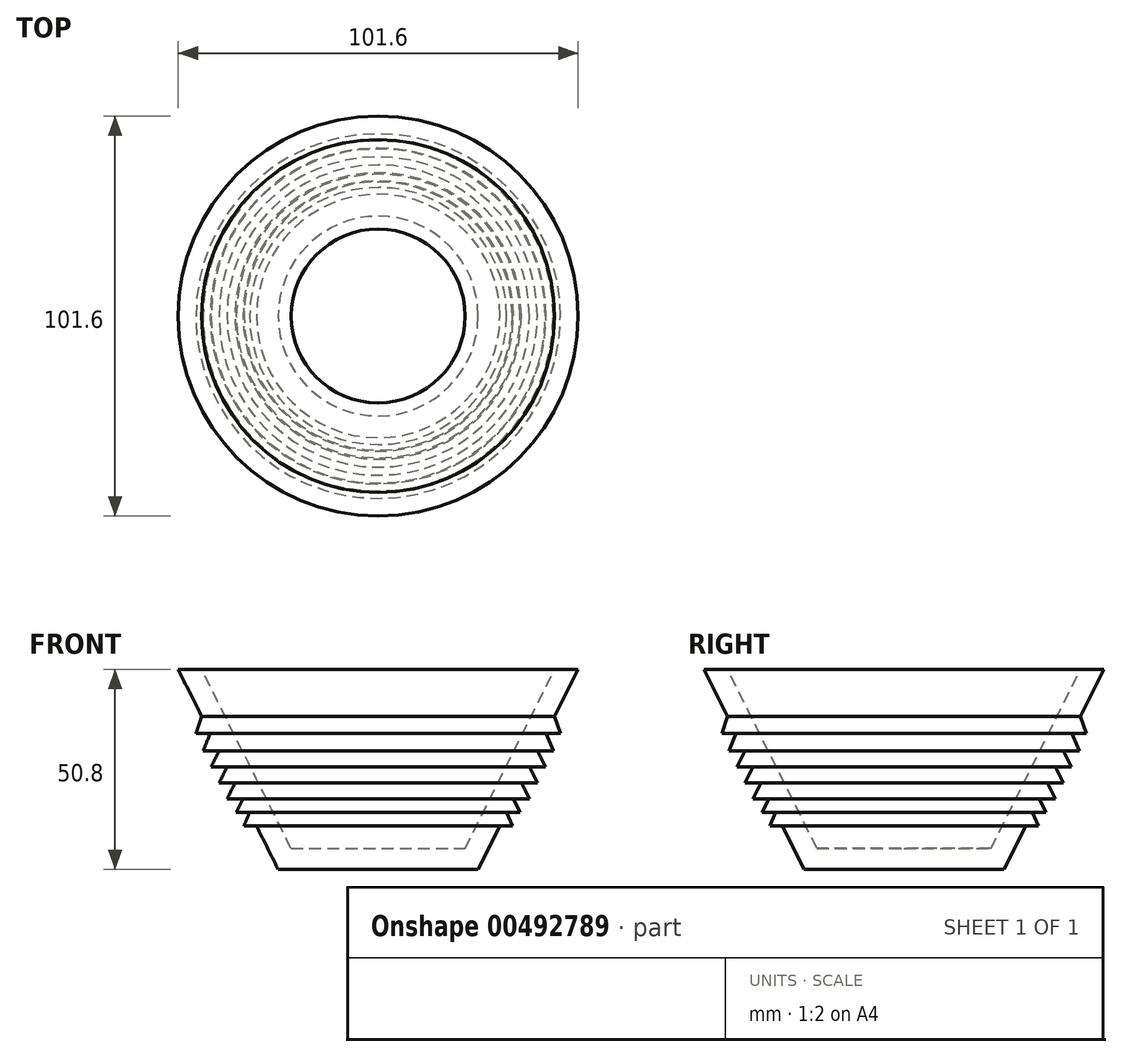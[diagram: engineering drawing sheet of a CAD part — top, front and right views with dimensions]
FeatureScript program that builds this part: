
annotation { "Feature Type Name" : "Feature", "Feature Type Description" : "" }
export const myFeature = defineFeature(function(context is Context, id is Id, definition is map)
    precondition{}
    {
        {
            var Q0;
            Q0=qCreatedBy(makeId("Front.planeOp"),FACE);
            var sketch = newSketch(context, id + "F0", { "sketchPlane" : qUnion([Q0])});
            skLineSegment(sketch, "E0", {"start": v(0, 0) * mm, "end": v(0, 50.8) * mm});
            skLineSegment(sketch, "E1", {"start": v(0, 0) * mm, "end": v(25.4, 0) * mm});
            skLineSegment(sketch, "E2", {"start": v(25.4, 0) * mm, "end": v(50.8, 50.8) * mm});
            skLineSegment(sketch, "E3.0", {"start": v(22.1, 5.33) * mm, "end": v(44.84, 50.8) * mm});
            skLineSegment(sketch, "E3.1", {"start": v(0, 5.33) * mm, "end": v(22.1, 5.33) * mm});
            skLineSegment(sketch, "E4", {"start": v(0, 5.33) * mm, "end": v(0, 0) * mm});
            skLineSegment(sketch, "E5", {"start": v(44.84, 50.8) * mm, "end": v(50.8, 50.8) * mm});
            skLineSegment(sketch, "E6", {"start": v(0, 0) * mm, "end": v(0, 50.8) * mm, "construction": true});
            skLineSegment(sketch, "E7", {"start": v(44.86, 38.92) * mm, "end": v(46.31, 34.53) * mm});
            skLineSegment(sketch, "E8", {"start": v(46.31, 34.53) * mm, "end": v(42.67, 34.53) * mm});
            skLineSegment(sketch, "E9", {"start": v(42.67, 34.53) * mm, "end": v(44.49, 30.07) * mm});
            skPoint(sketch, "E9.endSnap0", {"position": v(44.49, 34.53) * mm});
            skLineSegment(sketch, "E10", {"start": v(44.49, 30.07) * mm, "end": v(40.43, 30.07) * mm});
            skLineSegment(sketch, "E11", {"start": v(40.43, 30.07) * mm, "end": v(42.46, 26.01) * mm});
            skPoint(sketch, "E11.endSnap0", {"position": v(42.46, 30.07) * mm});
            skLineSegment(sketch, "E12", {"start": v(42.46, 26.01) * mm, "end": v(38.4, 26.01) * mm});
            skLineSegment(sketch, "E13", {"start": v(38.4, 26.01) * mm, "end": v(40.43, 21.96) * mm});
            skPoint(sketch, "E13.endSnap0", {"position": v(40.43, 26.01) * mm});
            skLineSegment(sketch, "E14", {"start": v(40.43, 21.96) * mm, "end": v(36.38, 21.96) * mm});
            skLineSegment(sketch, "E15", {"start": v(36.38, 21.96) * mm, "end": v(38.4, 17.9) * mm});
            skPoint(sketch, "E15.endSnap0", {"position": v(38.4, 21.96) * mm});
            skLineSegment(sketch, "E16", {"start": v(38.4, 17.9) * mm, "end": v(34.35, 17.9) * mm});
            skLineSegment(sketch, "E17", {"start": v(34.35, 17.9) * mm, "end": v(36.04, 14.52) * mm});
            skLineSegment(sketch, "E18", {"start": v(36.04, 14.52) * mm, "end": v(32.66, 14.52) * mm});
            skLineSegment(sketch, "E19", {"start": v(32.66, 14.52) * mm, "end": v(34.07, 11.06) * mm});
            skLineSegment(sketch, "E20", {"start": v(34.07, 11.06) * mm, "end": v(30.93, 11.06) * mm});
            skSolve(sketch);
        }
        {
            var Q0;
            Q0 = qSketchRegion(id + "F0", true);
            var Q1;
            Q1=sQuery(id+"F0.wireOp",EDGE,"E0");
            revolve(context, id + "F1", {"entities" : qUnion([Q0]), "axis" : qUnion([Q1]), "revolveType" : RevolveType.FULL});
        }
    });
